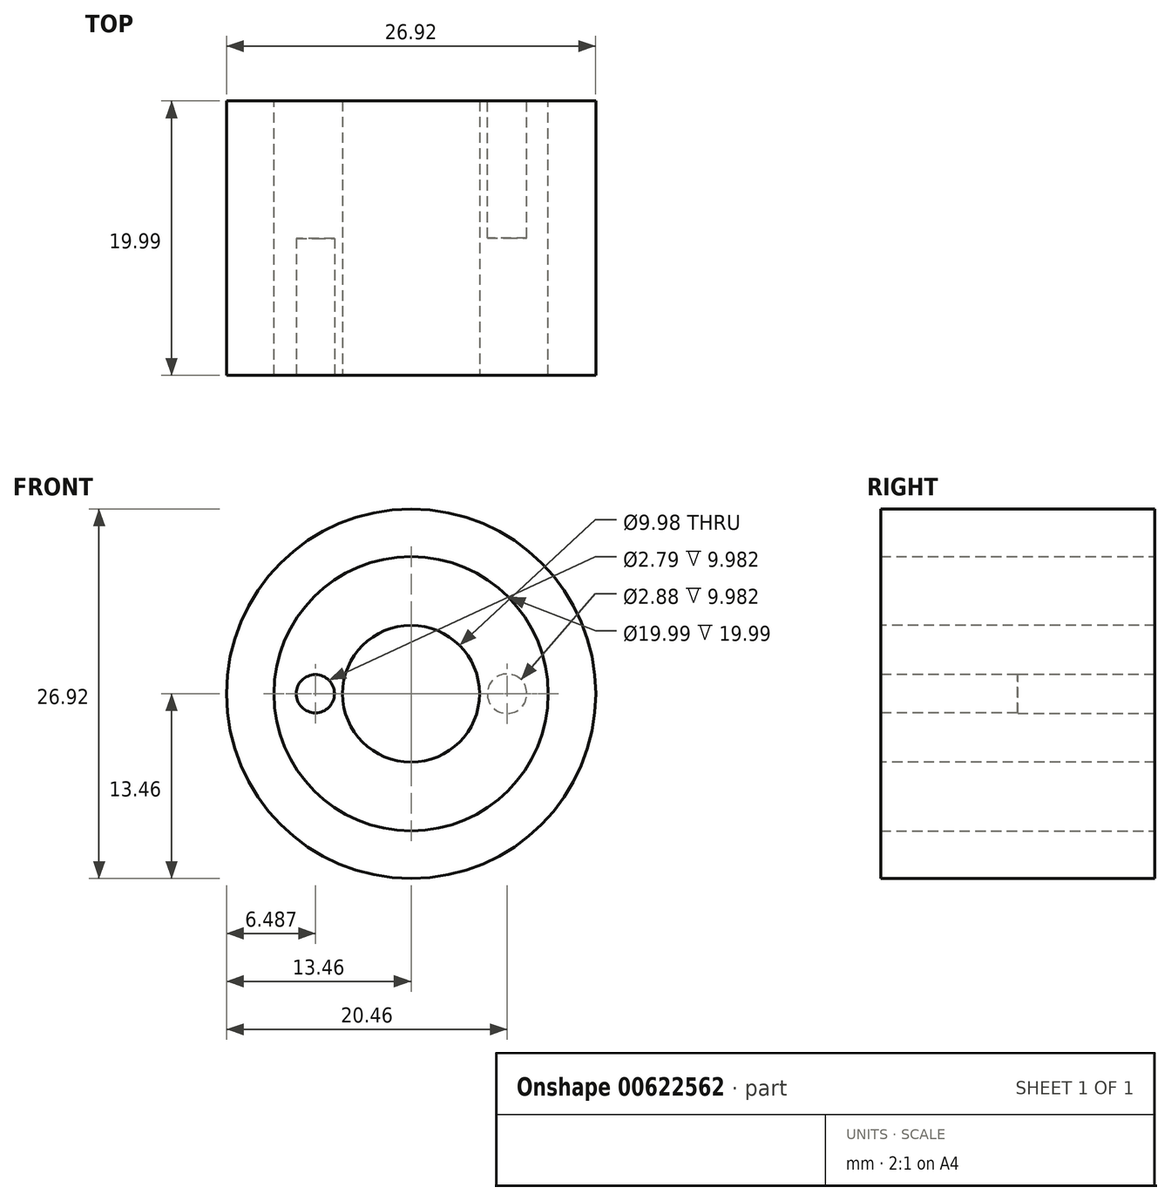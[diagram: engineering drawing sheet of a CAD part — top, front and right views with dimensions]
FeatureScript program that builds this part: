
annotation { "Feature Type Name" : "Feature", "Feature Type Description" : "" }
export const myFeature = defineFeature(function(context is Context, id is Id, definition is map)
    precondition{}
    {
        {
            var Q0;
            Q0=qCreatedBy(makeId("Front.planeOp"),FACE);
            var sketch = newSketch(context, id + "F0", { "sketchPlane" : qUnion([Q0])});
            skCircle(sketch, "E0", {"center": v(0, 0) * mm, "radius": 13.46 * mm});
            skSolve(sketch);
        }
        {
            var Q0;
            Q0 = qSketchRegion(id + "F0", true);
            extrude(context, id + "F1", {"entities" : qUnion([Q0]), "depth" : 19.99 * mm, "offsetDistance" : 25.4 * mm});
        }
        {
            var Q0;
            Q0=qCreatedBy(makeId("Front.planeOp"),FACE);
            var sketch = newSketch(context, id + "F2", { "sketchPlane" : qUnion([Q0])});
            skCircle(sketch, "E1", {"center": v(0, 0) * mm, "radius": 10 * mm});
            skSolve(sketch);
        }
        {
            var Q0;
            Q0 = qSketchRegion(id + "F2", true);
            extrude(context, id + "F3", {"entities" : qUnion([Q0]), "operationType" : NewBodyOperationType.REMOVE, "depth" : 25.4 * mm, "offsetDistance" : 25.4 * mm});
        }
        {
            var Q0;
            Q0=qCreatedBy(makeId("Front.planeOp"),FACE);
            var sketch = newSketch(context, id + "F4", { "sketchPlane" : qUnion([Q0])});
            skCircle(sketch, "E2", {"center": v(0, 0) * mm, "radius": 10 * mm});
            skSolve(sketch);
        }
        {
            var Q0;
            Q0 = qSketchRegion(id + "F4", true);
            extrude(context, id + "F5", {"entities" : qUnion([Q0]), "depth" : 19.99 * mm, "offsetDistance" : 25.4 * mm});
        }
        {
            var Q0;
            Q0=makeQuery(id+"F5.opExtrude","CAP_FACE",FACE,{"disambiguationData":[OSD([sQuery(id+"F4.wireOp",EDGE,"E2")])],"isStart":false});
            var sketch = newSketch(context, id + "F6", { "sketchPlane" : qUnion([Q0])});
            skPoint(sketch, "E3", {"position": v(0, 0) * mm});
            skSolve(sketch);
        }
        {
            var Q0;
            Q0=sQuery(id+"F6.wireOp",VERTEX,"E3");
            var Q1;
            Q1=makeQuery(id+"F5.opExtrude","SWEPT_BODY",BODY,{"disambiguationData":[OSD([sQuery(id+"F4.wireOp",EDGE,"E2")])]});
            hole(context, id + "F7", {"style" : HoleStyle.SIMPLE, "endStyle" : HoleEndStyle.THROUGH, "holeDiameter" : 9.98 * mm, "majorDiameter" : 6.35 * mm, "isTappedThrough" : true, "tappedDepth" : 12.7 * mm, "tapClearance" : 3, "locations" : qUnion([Q0]), "scope" : qUnion([Q1])});
        }
        {
            var Q0;
            Q0=makeQuery(id+"F5.opExtrude","CAP_FACE",FACE,{"disambiguationData":[OSD([sQuery(id+"F4.wireOp",EDGE,"E2")])],"isStart":false});
            var sketch = newSketch(context, id + "F8", { "sketchPlane" : qUnion([Q0])});
            skPoint(sketch, "E4", {"position": v(0, 0) * mm});
            skPoint(sketch, "E5", {"position": v(-6.98, 0) * mm});
            skSolve(sketch);
        }
        {
            var Q0;
            Q0=makeQuery(id+"F5.opExtrude","CAP_FACE",FACE,{"disambiguationData":[OSD([sQuery(id+"F4.wireOp",EDGE,"E2")])],"isStart":false});
            var sketch = newSketch(context, id + "F9", { "sketchPlane" : qUnion([Q0])});
            skSolve(sketch);
        }
        {
            var Q0;
            Q0=makeQuery(id+"F8.imprint","IMPRINT",FACE,{"disambiguationData":[TD([[makeQuery(id+"F8.imprint","IMPRINT",EDGE,{"derivedFrom":makeQuery(id+"F5.opExtrude","CAP_EDGE",EDGE,{"disambiguationData":[OSD([sQuery(id+"F4.wireOp",EDGE,"E2")])],"isStart":false})}),1.0]])]});
            var sketch = newSketch(context, id + "F10", { "sketchPlane" : qUnion([Q0])});
            skCircle(sketch, "E6", {"center": v(-6.97, 0) * mm, "radius": 1.4 * mm});
            skSolve(sketch);
        }
        {
            var Q0;
            Q0 = qSketchRegion(id + "F10", true);
            extrude(context, id + "F11", {"entities" : qUnion([Q0]), "operationType" : NewBodyOperationType.REMOVE, "oppositeDirection" : true, "depth" : 9.98 * mm, "offsetDistance" : 25.4 * mm});
        }
        {
            var Q0;
            Q0=makeQuery(id+"F0.imprint","IMPRINT",FACE,{"disambiguationData":[TD([[makeQuery(id+"F0.imprint","IMPRINT",EDGE,{"derivedFrom":sQuery(id+"F0.wireOp",EDGE,"E0")}),1.0]])]});
            var sketch = newSketch(context, id + "F12", { "sketchPlane" : qUnion([Q0])});
            skPoint(sketch, "E7", {"position": v(0, 0) * mm});
            skPoint(sketch, "E8", {"position": v(7, 0) * mm});
            skCircle(sketch, "E9", {"center": v(7, 0) * mm, "radius": 1.44 * mm});
            skSolve(sketch);
        }
        {
            var Q0;
            Q0 = qSketchRegion(id + "F12", true);
            extrude(context, id + "F13", {"entities" : qUnion([Q0]), "operationType" : NewBodyOperationType.REMOVE, "depth" : 9.98 * mm, "offsetDistance" : 25.4 * mm});
        }
    });
